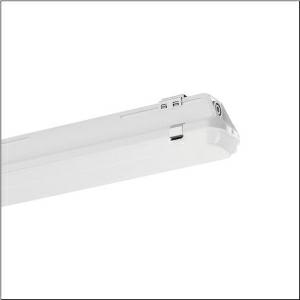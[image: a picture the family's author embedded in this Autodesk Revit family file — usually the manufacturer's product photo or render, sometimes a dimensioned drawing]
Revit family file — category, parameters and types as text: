
# Revit family: monsun_r__12_51fp10dp4b0q_a8e0
name_source: partatom
category: Lighting Fixtures
units: mm (PartAtom-declared; Revit-internal decimal feet)

## family parameters
Cut with Voids When Loaded = No
Host = Face
Light Source = No
Part Type = Normal
Room Calculation Point = No
Round Connector Dimension = Use Diameter
Shared = No

## types (1)
- --- (1 x LED, 12110 lm, 67.6 W, 4000K)
    Apparent Load = 68 VA
    CIE Flux Codes = 47 76 93 94 100
    Color Rendering = 80
    Color Temperature = 4000K
    Default Elevation = 1800 mm
    Description = Monsun® 12, damp-proof luminaire, chain hanger, primary optical cover: enclosure, of PMMA, light emission: direct distribution, primary light characteristic: symmetric, installation type: suspended mounting, surface-mounted, horizontal mounting, vertical mounting, LED rated luminous flux: 12.110 lm, light colour: 840, colour temperature: 4000K, control gear: ECG DALI, with terminal, 5-pole, max. 2.5mm², mains connection: 220..240V, AC, 50/60Hz, rated input power: 68W, luminaire housing, of glass-fibre reinforced polyester, uncoated, bright grey, length: 1.590 mm, width: 90 mm, height: 88mm, clip for enclosure, of stainless steel (V2A), ceiling mounting element, of stainless steel (V2A), chain hanger, of stainless steel (V2A), protection rating (complete): IP66, insulation class (complete): insulation class I (protective earthing), certification: CE, ENEC, VDE, protection symbol: D, impact resistance: IK04, permissible ambient temperature for indoor applications: -40..+35°C, standard: EN 50419, EN 60598-2-1, no direct snow, no direct sun, no direct rain, for indoor or canopied outdoor use, corresponds to IFS (International Featured Standards) requirements for safety and quality in the food industry, for animal farming (ammonia tested): for use in cowhouse, pig house, horse-stables... (not for use in poultry stables), AT max for animal farming = 40°C, packaging unit: 1 piece
    Height = 89 mm
    Lamp = 1 x LED
    Lamp Light Flux = 12110 lm
    Lamp Power = 67.6 W
    Lamp count = 1
    Length = 1590 mm
    Luminous efficacy = 179 lm/W
    Manufacturer = Siteco
    ModVariant = No
    Model = 51FP10DP4B0Q
    Mounting Place = Ceiling
    Mounting Type = Pendant
    Number of Poles = 1
    OnlyDefault = Yes
    Power Factor = 1
    Product Name = Monsun® 12
    Product group = damp-proof luminaire | ceiling pendant
    ProductGroupID = 908
    Protection Class = Protection class I
    Protection Degree = IP 66
    RLX_Detail_Level = 1
    RlxData = <blob elided: 92177 chars, md5=c796f542>
    Socket = socket
    Standby Power = 0 W
    System Light Flux = 12110 lm
    System Power = 68 W
    Type Comments = factory setting: luminous flux: 100 % | dim-lin: 254 | 389 mA
    Type Image = l_1004748.jpg
    URL = http://relux.com
    VarID = @adj_136037
    Voltage = 0 V
    Weight = 0.00 kg
    Width = 90 mm

## geometry (parser evidence)
native form markers: Blend x4, Sweep x13
no freeform markers — native parametric forms only
